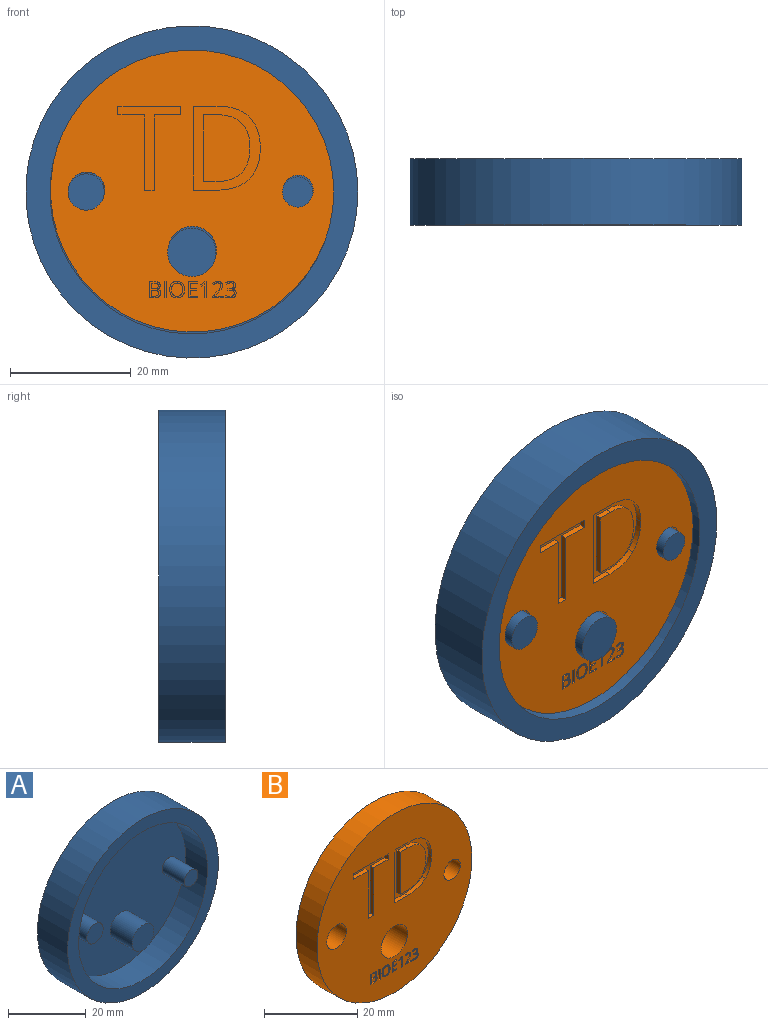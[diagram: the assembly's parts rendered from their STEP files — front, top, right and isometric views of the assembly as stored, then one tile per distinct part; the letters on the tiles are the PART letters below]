
ASSEMBLY  parts=2 mates=1
PART A: 11 faces, bbox 55x11x55 mm
  f0: cylinder r=27.5mm len=55mm, axis (0,1,0), area 1900.7mm2, adj f1,f2
  f1: plane 55x55mm, normal (0,-1,0), area 640.9mm2, adj f0,f3
  f2: plane 55x55mm, normal (0,1,0), area 2375.8mm2, adj f0
  f3: cylinder r=23.5mm len=47mm, axis (0,-1,0), area 1181.2mm2, adj f1,f4
  f4: plane 47x47mm, normal (0,-1,0), area 1636.8mm2, adj f3,f5,f7,f9
  f5: cylinder r=4mm len=8mm, axis (0,1,0), area 201.1mm2, adj f4,f6
  f6: plane 8x8mm, normal (0,-1,0), area 50.3mm2, adj f5
  f7: cylinder r=3mm len=8mm, axis (0,1,0), area 150.8mm2, adj f4,f8
  f8: plane 6x6mm, normal (0,-1,0), area 28.3mm2, adj f7
  f9: cylinder r=2.5mm len=8mm, axis (0,1,0), area 125.7mm2, adj f4,f10
  f10: plane 5x5mm, normal (0,-1,0), area 19.6mm2, adj f9
PART B: 155 faces, bbox 47x6.4x47 mm
  f0: plane 47x47mm, normal (0,-1,0), area 1448.4mm2, adj f1,f3,f4,f5,f6,f7,f8,f9
  f1: cylinder r=23.5mm len=47mm, axis (0,1,0), area 937.6mm2, adj f0,f2
  f2: plane 47x47mm, normal (0,1,0), area 1636.8mm2, adj f1,f3,f4,f5
  f3: cylinder r=4mm len=8mm, axis (0,-1,0), area 159.6mm2, adj f0,f2
  f4: cylinder r=3mm len=6.35mm, axis (0,-1,0), area 119.7mm2, adj f0,f2
  f5: cylinder r=2.5mm len=6.35mm, axis (0,-1,0), area 99.7mm2, adj f0,f2
  f6: plane 0.5x0.31mm, normal (0,0,1), area 0.2mm2, adj f0,f7,f9,f10
  f7: plane 2.68x0.5mm, normal (-1,0,0), area 1.3mm2, adj f0,f6,f8,f10
  f8: plane 0.5x0.31mm, normal (0,0,-1), area 0.2mm2, adj f0,f7,f9,f10
  f9: plane 2.68x0.5mm, normal (1,0,0), area 1.3mm2, adj f0,f6,f8,f10
  f10: plane 2.68x0.31mm, normal (0,-1,0), area 0.8mm2, adj f6,f7,f8,f9
  f11: plane 0.5x0.28mm, normal (-1,0,0), area 0.1mm2, adj f0,f12,f22,f23
  f12: plane 1.18x0.5mm, normal (0,0,-1), area 0.6mm2, adj f0,f11,f13,f23
  f13: plane 0.99x0.5mm, normal (-1,0,0), area 0.5mm2, adj f0,f12,f14,f23
  f14: plane 1.11x0.5mm, normal (0,0,1), area 0.6mm2, adj f0,f13,f15,f23
  f15: plane 0.5x0.28mm, normal (-1,0,0), area 0.1mm2, adj f0,f14,f16,f23
  f16: plane 1.11x0.5mm, normal (0,0,-1), area 0.6mm2, adj f0,f15,f17,f23
  f17: plane 0.86x0.5mm, normal (-1,0,0), area 0.4mm2, adj f0,f16,f18,f23
  f18: plane 1.18x0.5mm, normal (0,0,1), area 0.6mm2, adj f0,f17,f19,f23
  f19: plane 0.5x0.28mm, normal (-1,0,0), area 0.1mm2, adj f0,f18,f20,f23
  f20: plane 1.49x0.5mm, normal (0,0,-1), area 0.7mm2, adj f0,f19,f21,f23
  f21: plane 2.68x0.5mm, normal (1,0,0), area 1.3mm2, adj f0,f20,f22,f23
  f22: plane 1.49x0.5mm, normal (0,0,1), area 0.7mm2, adj f0,f11,f21,f23
  f23: plane 2.68x1.49mm, normal (0,-1,0), area 1.8mm2, adj f11,f12,f13,f14,f15,f16,f17,f18
  f24: plane 2.68x0.5mm, normal (-1,0,0), area 1.3mm2, adj f0,f25,f32,f33
  f25: plane 0.5x0.26mm, normal (0,0,-1), area 0.1mm2, adj f0,f24,f26,f33
  f26: plane 0.71x0.55mm, normal (0.61,0,-0.79), area 0.4mm2, adj f0,f25,f27,f33
  f27: plane 0.5x0.21mm, normal (0.79,0,0.61), area 0.1mm2, adj f0,f26,f28,f33
  f28: extruded ~0.5x0.44mm, area 0.3mm2, adj f0,f27,f29,f33
  f29: extruded ~0.5x0.09mm, area 0.1mm2, adj f0,f28,f30,f33
  f30: extruded ~0.5x0.45mm, area 0.2mm2, adj f0,f29,f31,f33
  f31: plane 1.91x0.5mm, normal (1,0,0), area 1mm2, adj f0,f30,f32,f33
  f32: plane 0.5x0.3mm, normal (0,0,1), area 0.1mm2, adj f0,f24,f31,f33
  f33: plane 2.68x0.97mm, normal (0,-1,0), area 1mm2, adj f24,f25,f26,f27,f28,f29,f30,f31
  f34: plane 0.5x0.28mm, normal (-1,0,0), area 0.1mm2, adj f0,f35,f53,f54
  f35: plane 1.38x0.5mm, normal (0,0,-1), area 0.7mm2, adj f0,f34,f36,f54
  f36: plane 0.5x0.01mm, normal (-1,0,0), area 0mm2, adj f0,f35,f37,f54
  f37: plane 0.59x0.57mm, normal (-0.7,0,0.71), area 0.4mm2, adj f0,f36,f38,f54
  f38: extruded ~0.63x0.54mm, area 0.4mm2, adj f0,f37,f39,f54
  f39: extruded ~0.5x0.5mm, area 0.3mm2, adj f0,f38,f40,f54
  f40: extruded ~0.52x0.5mm, area 0.3mm2, adj f0,f39,f41,f54
  f41: extruded ~0.59x0.5mm, area 0.3mm2, adj f0,f40,f42,f54
  f42: extruded ~0.81x0.5mm, area 0.4mm2, adj f0,f41,f43,f54
  f43: plane 0.5x0.21mm, normal (0.79,0,0.61), area 0.1mm2, adj f0,f42,f44,f54
  f44: extruded ~0.5x0.33mm, area 0.2mm2, adj f0,f43,f45,f54
  f45: extruded ~0.5x0.32mm, area 0.2mm2, adj f0,f44,f46,f54
  f46: extruded ~0.5x0.36mm, area 0.2mm2, adj f0,f45,f47,f54
  f47: extruded ~0.5x0.34mm, area 0.2mm2, adj f0,f46,f48,f54
  f48: extruded ~0.5x0.28mm, area 0.1mm2, adj f0,f47,f49,f54
  f49: extruded ~0.5x0.27mm, area 0.2mm2, adj f0,f48,f50,f54
  f50: extruded ~0.5x0.47mm, area 0.3mm2, adj f0,f49,f51,f54
  f51: plane 0.71x0.71mm, normal (0.71,0,-0.71), area 0.5mm2, adj f0,f50,f52,f54
  f52: plane 0.5x0.26mm, normal (1,0,0), area 0.1mm2, adj f0,f51,f53,f54
  f53: plane 1.76x0.5mm, normal (0,0,1), area 0.9mm2, adj f0,f34,f52,f54
  f54: plane 2.72x1.76mm, normal (0,-1,0), area 1.6mm2, adj f34,f35,f36,f37,f38,f39,f40,f41
  f55: extruded ~0.5x0.49mm, area 0.3mm2, adj f0,f56,f82,f83
  f56: extruded ~0.61x0.5mm, area 0.3mm2, adj f0,f55,f57,f83
  f57: extruded ~0.5x0.45mm, area 0.2mm2, adj f0,f56,f58,f83
  f58: extruded ~0.5x0.38mm, area 0.2mm2, adj f0,f57,f59,f83
  f59: plane 0.5x0.21mm, normal (0.8,0,0.6), area 0.1mm2, adj f0,f58,f60,f83
  f60: extruded ~0.5x0.36mm, area 0.2mm2, adj f0,f59,f61,f83
  f61: extruded ~0.5x0.33mm, area 0.2mm2, adj f0,f60,f62,f83
  f62: extruded ~0.5x0.37mm, area 0.2mm2, adj f0,f61,f63,f83
  f63: extruded ~0.5x0.31mm, area 0.2mm2, adj f0,f62,f64,f83
  f64: extruded ~0.5x0.38mm, area 0.2mm2, adj f0,f63,f65,f83
  f65: extruded ~0.5x0.5mm, area 0.3mm2, adj f0,f64,f66,f83
  f66: plane 0.5x0.27mm, normal (0,0,-1), area 0.1mm2, adj f0,f65,f67,f83
  f67: plane 0.5x0.26mm, normal (1,0,0), area 0.1mm2, adj f0,f66,f68,f83
  f68: plane 0.5x0.26mm, normal (0,0,1), area 0.1mm2, adj f0,f67,f69,f83
  f69: extruded ~0.77x0.5mm, area 0.5mm2, adj f0,f68,f70,f83
  f70: extruded ~0.69x0.54mm, area 0.5mm2, adj f0,f69,f71,f83
  f71: extruded ~0.5x0.37mm, area 0.2mm2, adj f0,f70,f72,f83
  f72: extruded ~0.5x0.37mm, area 0.2mm2, adj f0,f71,f73,f83
  f73: plane 0.5x0.29mm, normal (1,0,0), area 0.1mm2, adj f0,f72,f74,f83
  f74: extruded ~0.5x0.34mm, area 0.2mm2, adj f0,f73,f75,f83
  f75: extruded ~0.5x0.39mm, area 0.2mm2, adj f0,f74,f76,f83
  f76: extruded ~0.76x0.5mm, area 0.4mm2, adj f0,f75,f77,f83
  f77: extruded ~0.59x0.5mm, area 0.3mm2, adj f0,f76,f78,f83
  f78: extruded ~0.5x0.43mm, area 0.2mm2, adj f0,f77,f79,f83
  f79: extruded ~0.5x0.48mm, area 0.3mm2, adj f0,f78,f80,f83
  f80: plane 0.5x0.01mm, normal (-1,0,0), area 0mm2, adj f0,f79,f81,f83
  f81: extruded ~0.5x0.41mm, area 0.2mm2, adj f0,f80,f82,f83
  f82: extruded ~0.5x0.42mm, area 0.2mm2, adj f0,f55,f81,f83
  f83: plane 2.76x1.75mm, normal (0,-1,0), area 1.7mm2, adj f55,f56,f57,f58,f59,f60,f61,f62
  f84: extruded ~1.01x0.5mm, area 0.5mm2, adj f0,f85,f99,f100
  f85: extruded ~0.9x0.5mm, area 0.5mm2, adj f0,f84,f86,f100
  f86: extruded ~0.92x0.5mm, area 0.5mm2, adj f0,f85,f87,f100
  f87: extruded ~1.01x0.5mm, area 0.5mm2, adj f0,f86,f88,f100
  f88: extruded ~1.02x0.5mm, area 0.5mm2, adj f0,f87,f89,f100
  f89: extruded ~0.91x0.5mm, area 0.5mm2, adj f0,f88,f90,f100
  f90: extruded ~0.9x0.5mm, area 0.5mm2, adj f0,f89,f99,f100
  f91: extruded ~0.82x0.5mm, area 0.4mm2, adj f92,f98,f100,f101
  f92: extruded ~0.68x0.5mm, area 0.4mm2, adj f91,f93,f100,f101
  f93: extruded ~0.67x0.5mm, area 0.4mm2, adj f92,f94,f100,f101
  f94: extruded ~0.82x0.5mm, area 0.4mm2, adj f93,f95,f100,f101
  f95: extruded ~0.83x0.5mm, area 0.4mm2, adj f94,f96,f100,f101
  f96: extruded ~0.67x0.5mm, area 0.4mm2, adj f95,f97,f100,f101
  f97: extruded ~0.67x0.5mm, area 0.4mm2, adj f96,f98,f100,f101
  f98: extruded ~0.83x0.5mm, area 0.4mm2, adj f91,f97,f100,f101
  f99: extruded ~1.01x0.5mm, area 0.5mm2, adj f0,f84,f90,f100
  f100: plane 2.76x2.47mm, normal (0,-1,0), area 2.3mm2, adj f84,f85,f86,f87,f88,f89,f90,f91
  f101: plane 2.21x1.81mm, normal (0,-1,0), area 3.3mm2, adj f91,f92,f93,f94,f95,f96,f97,f98
  f102: plane 2.68x0.5mm, normal (1,0,0), area 1.3mm2, adj f0,f103,f126,f127
  f103: plane 0.94x0.5mm, normal (0,0,1), area 0.5mm2, adj f0,f102,f104,f127
  f104: extruded ~0.68x0.5mm, area 0.4mm2, adj f0,f103,f105,f127
  f105: extruded ~0.56x0.5mm, area 0.3mm2, adj f0,f104,f106,f127
  f106: extruded ~0.64x0.61mm, area 0.5mm2, adj f0,f105,f107,f127
  f107: plane 0.5x0.02mm, normal (-1,0,0), area 0mm2, adj f0,f106,f108,f127
  f108: extruded ~0.5x0.39mm, area 0.2mm2, adj f0,f107,f109,f127
  f109: extruded ~0.5x0.39mm, area 0.2mm2, adj f0,f108,f110,f127
  f110: extruded ~0.5x0.5mm, area 0.3mm2, adj f0,f109,f111,f127
  f111: extruded ~0.77x0.5mm, area 0.4mm2, adj f0,f110,f126,f127
  f112: plane 0.88x0.5mm, normal (-1,0,0), area 0.4mm2, adj f113,f124,f127,f129
  f113: plane 0.5x0.46mm, normal (0,0,1), area 0.2mm2, adj f112,f114,f127,f129
  f114: extruded ~0.51x0.5mm, area 0.3mm2, adj f113,f115,f127,f129
  f115: extruded ~0.5x0.33mm, area 0.2mm2, adj f114,f116,f127,f129
  f116: extruded ~0.5x0.35mm, area 0.2mm2, adj f115,f117,f127,f129
  f117: extruded ~0.5x0.48mm, area 0.2mm2, adj f116,f124,f127,f129
  f118: plane 0.53x0.5mm, normal (0,0,1), area 0.3mm2, adj f119,f125,f127,f128
  f119: extruded ~0.51x0.5mm, area 0.3mm2, adj f118,f120,f127,f128
  f120: extruded ~0.5x0.37mm, area 0.2mm2, adj f119,f121,f127,f128
  f121: extruded ~0.5x0.39mm, area 0.2mm2, adj f120,f122,f127,f128
  f122: extruded ~0.5x0.49mm, area 0.3mm2, adj f121,f123,f127,f128
  f123: plane 0.56x0.5mm, normal (0,0,-1), area 0.3mm2, adj f122,f125,f127,f128
  f124: plane 0.51x0.5mm, normal (0,0,-1), area 0.3mm2, adj f112,f117,f127,f129
  f125: plane 1x0.5mm, normal (-1,0,0), area 0.5mm2, adj f118,f123,f127,f128
  f126: plane 0.76x0.5mm, normal (0,0,-1), area 0.4mm2, adj f0,f102,f111,f127
  f127: plane 2.68x1.86mm, normal (0,-1,0), area 2.4mm2, adj f102,f103,f104,f105,f106,f107,f108,f109
  f128: plane 1.21x1mm, normal (0,-1,0), area 1.1mm2, adj f118,f119,f120,f121,f122,f123,f125
  f129: plane 1.13x0.88mm, normal (0,-1,0), area 0.9mm2, adj f112,f113,f114,f115,f116,f117,f124
  f130: extruded ~5.01x1.79mm, area 5.5mm2, adj f0,f131,f143,f144
  f131: extruded ~5.03x1.79mm, area 5.5mm2, adj f0,f130,f132,f144
  f132: plane 4.25x1mm, normal (0,0,-1), area 4.3mm2, adj f0,f131,f133,f144
  f133: plane 13.88x1mm, normal (1,0,0), area 13.9mm2, adj f0,f132,f134,f144
  f134: plane 3.85x1mm, normal (0,0,1), area 3.8mm2, adj f0,f133,f135,f144
  f135: extruded ~5.37x1.82mm, area 5.8mm2, adj f0,f134,f143,f144
  f136: extruded ~4.2x1.45mm, area 4.6mm2, adj f137,f142,f144,f145
  f137: extruded ~4.34x1.42mm, area 4.7mm2, adj f136,f138,f144,f145
  f138: plane 1.97x1mm, normal (0,0,-1), area 2mm2, adj f137,f139,f144,f145
  f139: plane 11.09x1mm, normal (-1,0,0), area 11.1mm2, adj f138,f140,f144,f145
  f140: plane 2.34x1mm, normal (0,0,1), area 2.3mm2, adj f139,f141,f144,f145
  f141: extruded ~4.05x1.38mm, area 4.4mm2, adj f140,f142,f144,f145
  f142: extruded ~4.09x1.36mm, area 4.4mm2, adj f136,f141,f144,f145
  f143: extruded ~5.25x1.87mm, area 5.7mm2, adj f0,f130,f135,f144
  f144: plane 13.88x11.08mm, normal (0,-1,0), area 60.9mm2, adj f130,f131,f132,f133,f134,f135,f136,f137
  f145: plane 11.09x7.76mm, normal (0,-1,0), area 75.5mm2, adj f136,f137,f138,f139,f140,f141,f142
  f146: plane 12.44x1mm, normal (-1,0,0), area 12.4mm2, adj f0,f147,f153,f154
  f147: plane 4.4x1mm, normal (0,0,1), area 4.4mm2, adj f0,f146,f148,f154
  f148: plane 1.43x1mm, normal (-1,0,0), area 1.4mm2, adj f0,f147,f149,f154
  f149: plane 10.4x1mm, normal (0,0,-1), area 10.4mm2, adj f0,f148,f150,f154
  f150: plane 1.43x1mm, normal (1,0,0), area 1.4mm2, adj f0,f149,f151,f154
  f151: plane 4.4x1mm, normal (0,0,1), area 4.4mm2, adj f0,f150,f152,f154
  f152: plane 12.44x1mm, normal (1,0,0), area 12.4mm2, adj f0,f151,f153,f154
  f153: plane 1.61x1mm, normal (0,0,1), area 1.6mm2, adj f0,f146,f152,f154
  f154: plane 13.88x10.4mm, normal (0,-1,0), area 35mm2, adj f146,f147,f148,f149,f150,f151,f152,f153
PLACE A t=(-42.94,-21.66,-4.95)mm
PLACE B t=(-42.84,-24.66,-4.64)mm
MATE fastened A.f4 <-> B.f1  axis (0,-1,0) through (-42.84,-24.66,-4.64)mm
